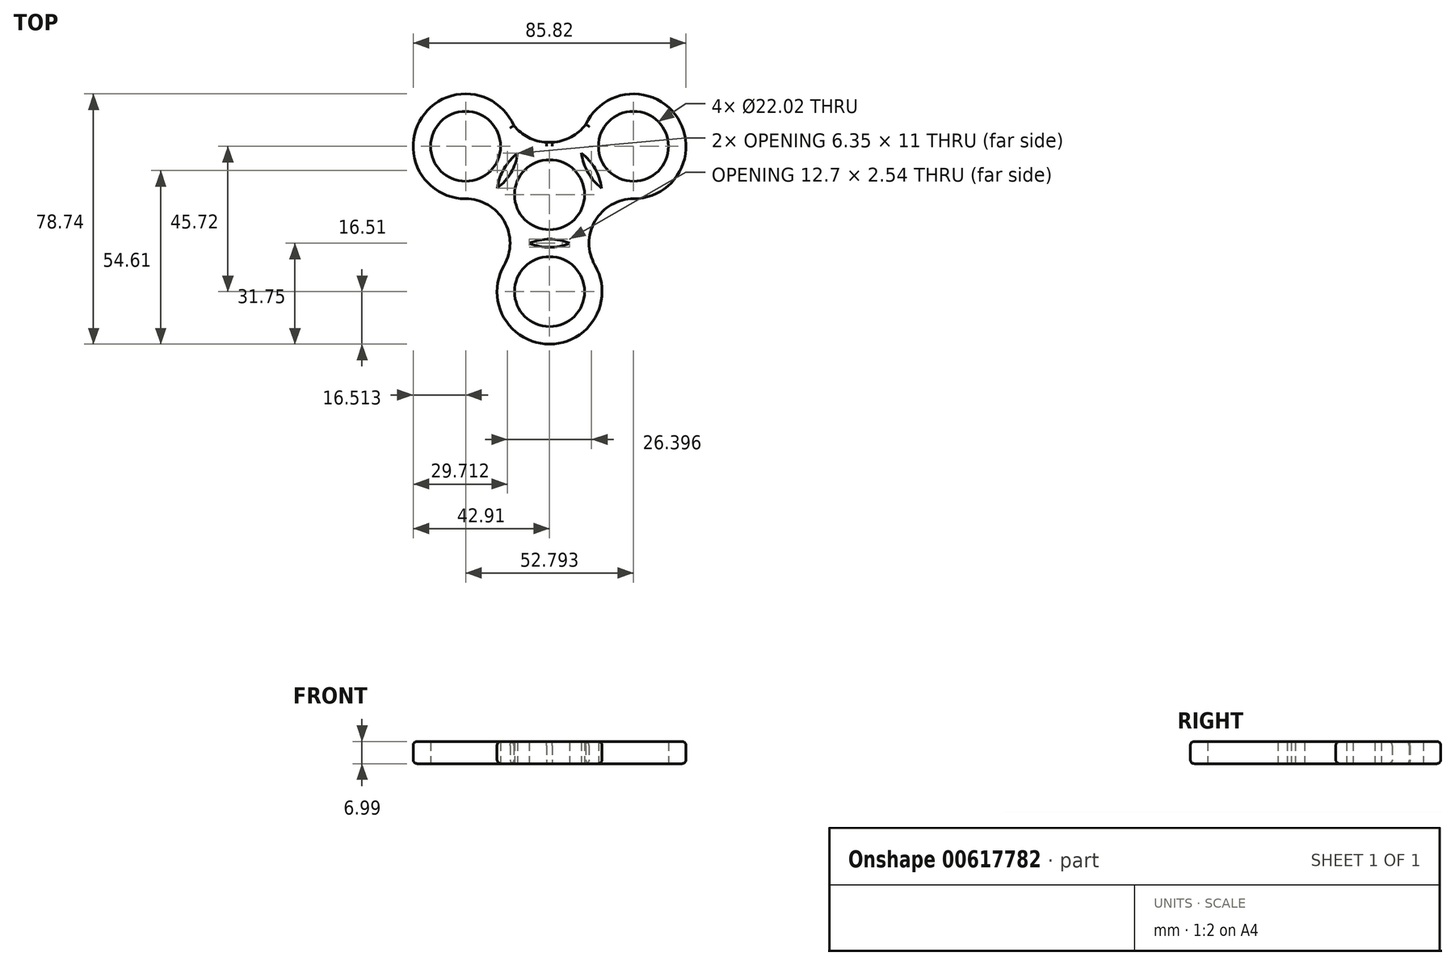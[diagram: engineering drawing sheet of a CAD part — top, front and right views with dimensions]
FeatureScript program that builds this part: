
annotation { "Feature Type Name" : "Feature", "Feature Type Description" : "" }
export const myFeature = defineFeature(function(context is Context, id is Id, definition is map)
    precondition{}
    {
        {
            var Q0;
            Q0=qCreatedBy(makeId("Top.planeOp"),FACE);
            var sketch = newSketch(context, id + "F0", { "sketchPlane" : qUnion([Q0])});
            skCircle(sketch, "E0", {"center": v(0, 0) * mm, "radius": 11.01 * mm});
            skLineSegment(sketch, "E1", {"start": v(0, 0) * mm, "end": v(0, -30.48) * mm});
            skLineSegment(sketch, "E2", {"start": v(0, 0) * mm, "end": v(-26.4, 15.24) * mm});
            skLineSegment(sketch, "E3", {"start": v(0, 0) * mm, "end": v(26.4, 15.24) * mm});
            skCircle(sketch, "E4", {"center": v(0, -30.48) * mm, "radius": 11.01 * mm});
            skCircle(sketch, "E5", {"center": v(26.4, 15.24) * mm, "radius": 11.01 * mm});
            skCircle(sketch, "E6", {"center": v(-26.4, 15.24) * mm, "radius": 11.01 * mm});
            skCircle(sketch, "E7", {"center": v(-26.4, 15.24) * mm, "radius": 16.51 * mm});
            skCircle(sketch, "E8", {"center": v(0, 0) * mm, "radius": 16.51 * mm});
            skCircle(sketch, "E9", {"center": v(26.4, 15.24) * mm, "radius": 16.51 * mm});
            skCircle(sketch, "E10", {"center": v(0, -30.48) * mm, "radius": 16.51 * mm});
            skArc(sketch, "E11", {"start": v(-14.3, -22.23) * mm, "mid": v(-14.3, -8.26) * mm, "end": v(-26.4, -1.27) * mm});
            skArc(sketch, "E12", {"start": v(26.4, -1.27) * mm, "mid": v(14.3, -8.26) * mm, "end": v(14.3, -22.22) * mm});
            skArc(sketch, "E13", {"start": v(-11.24, 21.78) * mm, "mid": v(0.17, 16.46) * mm, "end": v(11.4, 22.14) * mm});
            skSolve(sketch);
        }
        {
            var Q0;
            Q0 = qSketchRegion(id + "F0", true);
            extrude(context, id + "F1", {"entities" : qUnion([Q0]), "depth" : 7 * mm, "offsetDistance" : 25.4 * mm});
        }
        {
            var Q0;
            {var subQ0=sQuery(id+"F0.wireOp",EDGE,"E7");Q0=makeQuery(id+"F1.opExtrude","CAP_EDGE",EDGE,{"disambiguationData":[OSD([subQ0]),TDD([makeQuery(id+"F0.imprint","IMPRINT",EDGE,{"disambiguationData":[TD([[makeQuery(id+"F0.imprint","INTERSECT",VERTEX,{"derivedFrom":[subQ0,sQuery(id+"F0.wireOp",EDGE,"E11")]}),1.0]])],"derivedFrom":subQ0})])],"isStart":false});}
            var Q1;
            {var subQ0=sQuery(id+"F0.wireOp",EDGE,"E13");Q1=makeQuery(id+"F1.opExtrude","CAP_EDGE",EDGE,{"disambiguationData":[OSD([subQ0]),TDD([makeQuery(id+"F0.imprint","IMPRINT",EDGE,{"disambiguationData":[TD([[makeQuery(id+"F0.imprint","INTERSECT",VERTEX,{"derivedFrom":[sQuery(id+"F0.wireOp",EDGE,"E9"),subQ0]}),1.0]])],"derivedFrom":subQ0})])],"isStart":false});}
            var Q2;
            {var subQ0=sQuery(id+"F0.wireOp",EDGE,"E9");Q2=makeQuery(id+"F1.opExtrude","CAP_EDGE",EDGE,{"disambiguationData":[OSD([subQ0]),TDD([makeQuery(id+"F0.imprint","IMPRINT",EDGE,{"disambiguationData":[TD([[makeQuery(id+"F0.imprint","INTERSECT",VERTEX,{"derivedFrom":[subQ0,sQuery(id+"F0.wireOp",EDGE,"E12")]}),-1.0]])],"derivedFrom":subQ0})])],"isStart":false});}
            var Q3;
            {var subQ0=sQuery(id+"F0.wireOp",EDGE,"E13");Q3=makeQuery(id+"F1.opExtrude","CAP_EDGE",EDGE,{"disambiguationData":[OSD([subQ0]),TDD([makeQuery(id+"F0.imprint","IMPRINT",EDGE,{"disambiguationData":[TD([[makeQuery(id+"F0.imprint","INTERSECT",VERTEX,{"derivedFrom":[sQuery(id+"F0.wireOp",EDGE,"E7"),subQ0]}),-1.0]])],"derivedFrom":subQ0})])],"isStart":false});}
            var Q4;
            {var subQ0=sQuery(id+"F0.wireOp",EDGE,"E13");var subQ1=sQuery(id+"F0.wireOp",EDGE,"E8");Q4=makeQuery(id+"F1.opExtrude","CAP_EDGE",EDGE,{"disambiguationData":[OSD([subQ1]),TDD([makeQuery(id+"F0.imprint","IMPRINT",EDGE,{"disambiguationData":[TD([[makeQuery(id+"F0.imprint","INTERSECT",VERTEX,{"disambiguationData":[OD(0.0)],"derivedFrom":[subQ1,subQ0]}),-1.0]])],"derivedFrom":subQ1})])],"isStart":false});}
            fillet(context, id + "F2", {"entities" : qUnion([Q0, Q1, Q2, Q3, Q4]), "radius" : 1.27 * mm, "tangentPropagation" : true, "allowEdgeOverflow" : false});
        }
        {
            var Q0;
            {var subQ0=sQuery(id+"F0.wireOp",EDGE,"E9");Q0=makeQuery(id+"F1.opExtrude","CAP_EDGE",EDGE,{"disambiguationData":[OSD([subQ0]),TDD([makeQuery(id+"F0.imprint","IMPRINT",EDGE,{"disambiguationData":[TD([[makeQuery(id+"F0.imprint","INTERSECT",VERTEX,{"derivedFrom":[subQ0,sQuery(id+"F0.wireOp",EDGE,"E12")]}),-1.0]])],"derivedFrom":subQ0})])],"isStart":true});}
            var Q1;
            {var subQ0=sQuery(id+"F0.wireOp",EDGE,"E13");Q1=makeQuery(id+"F1.opExtrude","CAP_EDGE",EDGE,{"disambiguationData":[OSD([subQ0]),TDD([makeQuery(id+"F0.imprint","IMPRINT",EDGE,{"disambiguationData":[TD([[makeQuery(id+"F0.imprint","INTERSECT",VERTEX,{"derivedFrom":[sQuery(id+"F0.wireOp",EDGE,"E9"),subQ0]}),1.0]])],"derivedFrom":subQ0})])],"isStart":true});}
            var Q2;
            {var subQ0=sQuery(id+"F0.wireOp",EDGE,"E13");Q2=makeQuery(id+"F1.opExtrude","CAP_EDGE",EDGE,{"disambiguationData":[OSD([subQ0]),TDD([makeQuery(id+"F0.imprint","IMPRINT",EDGE,{"disambiguationData":[TD([[makeQuery(id+"F0.imprint","INTERSECT",VERTEX,{"derivedFrom":[sQuery(id+"F0.wireOp",EDGE,"E7"),subQ0]}),-1.0]])],"derivedFrom":subQ0})])],"isStart":true});}
            var Q3;
            {var subQ0=sQuery(id+"F0.wireOp",EDGE,"E13");var subQ1=sQuery(id+"F0.wireOp",EDGE,"E8");Q3=makeQuery(id+"F1.opExtrude","CAP_EDGE",EDGE,{"disambiguationData":[OSD([subQ1]),TDD([makeQuery(id+"F0.imprint","IMPRINT",EDGE,{"disambiguationData":[TD([[makeQuery(id+"F0.imprint","INTERSECT",VERTEX,{"disambiguationData":[OD(0.0)],"derivedFrom":[subQ1,subQ0]}),-1.0]])],"derivedFrom":subQ1})])],"isStart":true});}
            fillet(context, id + "F3", {"entities" : qUnion([Q0, Q1, Q2, Q3]), "radius" : 1.27 * mm, "tangentPropagation" : true, "allowEdgeOverflow" : false});
        }
    });
